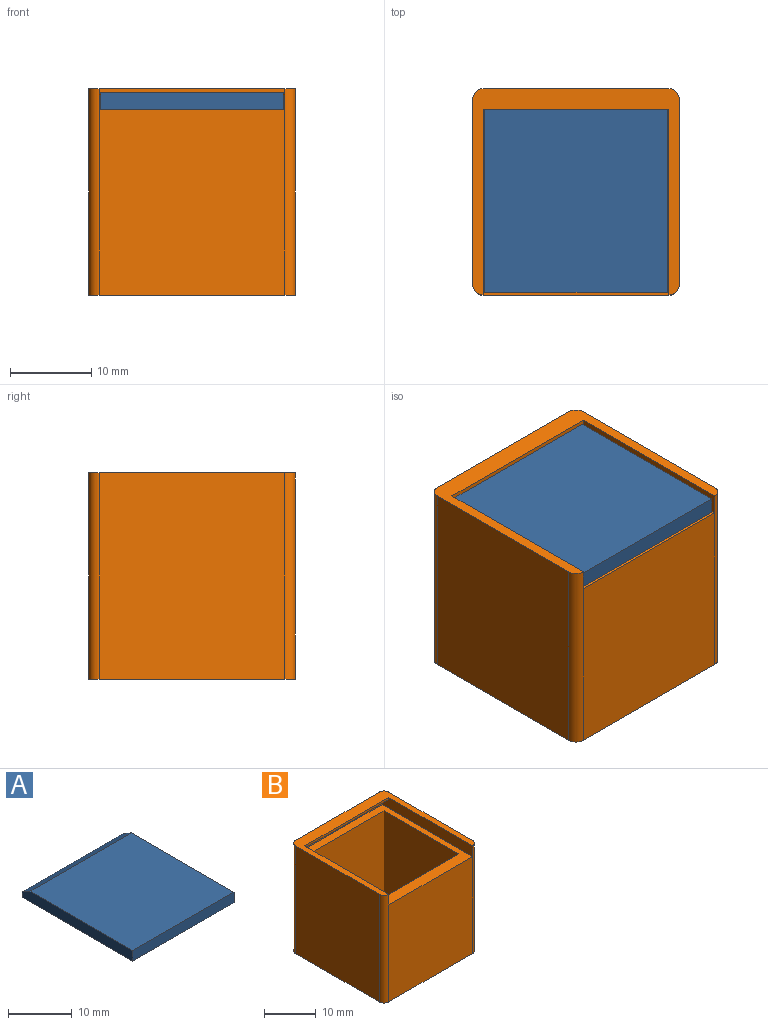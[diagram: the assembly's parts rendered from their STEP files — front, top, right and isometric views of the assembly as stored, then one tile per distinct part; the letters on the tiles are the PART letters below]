
ASSEMBLY  parts=2 mates=1
PART A: 7 faces, bbox 22.5x24.6x2 mm
  f0: plane 22.5x2.03mm, normal (0,-1,0), area 45.7mm2, adj f1,f3,f5,f6
  f1: plane 24.64x22.5mm, normal (0,0,-1), area 554.5mm2, adj f0,f2,f5,f6
  f2: plane 22.5x1.01mm, normal (0,1,0), area 22.6mm2, adj f1,f4,f5,f6
  f3: plane 22.86x22.5mm, normal (0,0,1), area 514.5mm2, adj f0,f4,f5,f6
  f4: plane 22.5x1.78mm, normal (0,0.5,0.87), area 46.2mm2, adj f2,f3,f5,f6
  f5: plane 24.64x2.03mm, normal (-1,0,0), area 49.2mm2, adj f0,f1,f2,f3,f4
  f6: plane 24.64x2.03mm, normal (1,0,0), area 49.2mm2, adj f0,f1,f2,f3,f4
PART B: 21 faces, bbox 25.4x25.4x25.4 mm
  f0: plane 20.32x20.32mm, normal (0,-1,0), area 412.9mm2, adj f8,f10,f11,f14
  f1: plane 22.86x22.86mm, normal (0,-1,0), area 522.6mm2, adj f3,f14,f19,f20
  f2: plane 25.4x25.4mm, normal (0,0,1), area 121.2mm2, adj f4,f5,f6,f9,f12,f13,f17,f18
  f3: plane 25.4x25.4mm, normal (0,0,-1), area 643.8mm2, adj f1,f4,f5,f6,f17,f18,f19,f20
  f4: plane 25.4x22.86mm, normal (1,0,0), area 580.6mm2, adj f2,f3,f18,f20
  f5: plane 25.4x22.86mm, normal (-1,0,0), area 580.6mm2, adj f2,f3,f17,f19
  f6: plane 25.4x22.86mm, normal (0,1,0), area 580.6mm2, adj f2,f3,f17,f18
  f7: plane 20.32x20.32mm, normal (0,1,0), area 412.9mm2, adj f8,f10,f11,f14
  f8: plane 20.32x20.32mm, normal (-1,0,0), area 412.9mm2, adj f0,f7,f11,f14
  f9: plane 22.86x0.51mm, normal (0,-1,0), area 11.6mm2, adj f2,f12,f13,f16
  f10: plane 20.32x20.32mm, normal (1,0,0), area 412.9mm2, adj f0,f7,f11,f14
  f11: plane 20.32x20.32mm, normal (0,0,1), area 412.9mm2, adj f0,f7,f8,f10
  f12: plane 24.64x2.54mm, normal (-1,0,0), area 60.8mm2, adj f2,f9,f14,f15,f16,f20
  f13: plane 24.64x2.54mm, normal (1,0,0), area 60.8mm2, adj f2,f9,f14,f15,f16,f19
  f14: plane 24.64x22.86mm, normal (0,0,1), area 150.3mm2, adj f0,f1,f7,f8,f10,f12,f13,f15
  f15: plane 22.86x1.01mm, normal (0,-1,0), area 23mm2, adj f12,f13,f14,f16
  f16: plane 22.86x1.78mm, normal (0,-0.5,-0.87), area 46.9mm2, adj f9,f12,f13,f15
  f17: cylinder r=1.27mm len=25.4mm, axis (0,0,-1), area 50.7mm2, adj f2,f3,f5,f6
  f18: cylinder r=1.27mm len=25.4mm, axis (0,0,1), area 50.7mm2, adj f2,f3,f4,f6
  f19: cylinder r=1.27mm len=25.4mm, axis (0,0,1), area 50.7mm2, adj f1,f2,f3,f5,f13
  f20: cylinder r=1.27mm len=25.4mm, axis (0,0,-1), area 50.7mm2, adj f1,f2,f3,f4,f12
PLACE A t=(-258.59,-108.99,136.08)mm
PLACE B t=(-258.59,-108.54,124.65)mm fixed
MATE slider B.f15 <-> A.f2  axis (0,-1,0) through (-258.59,-109.3,135.32)mm
